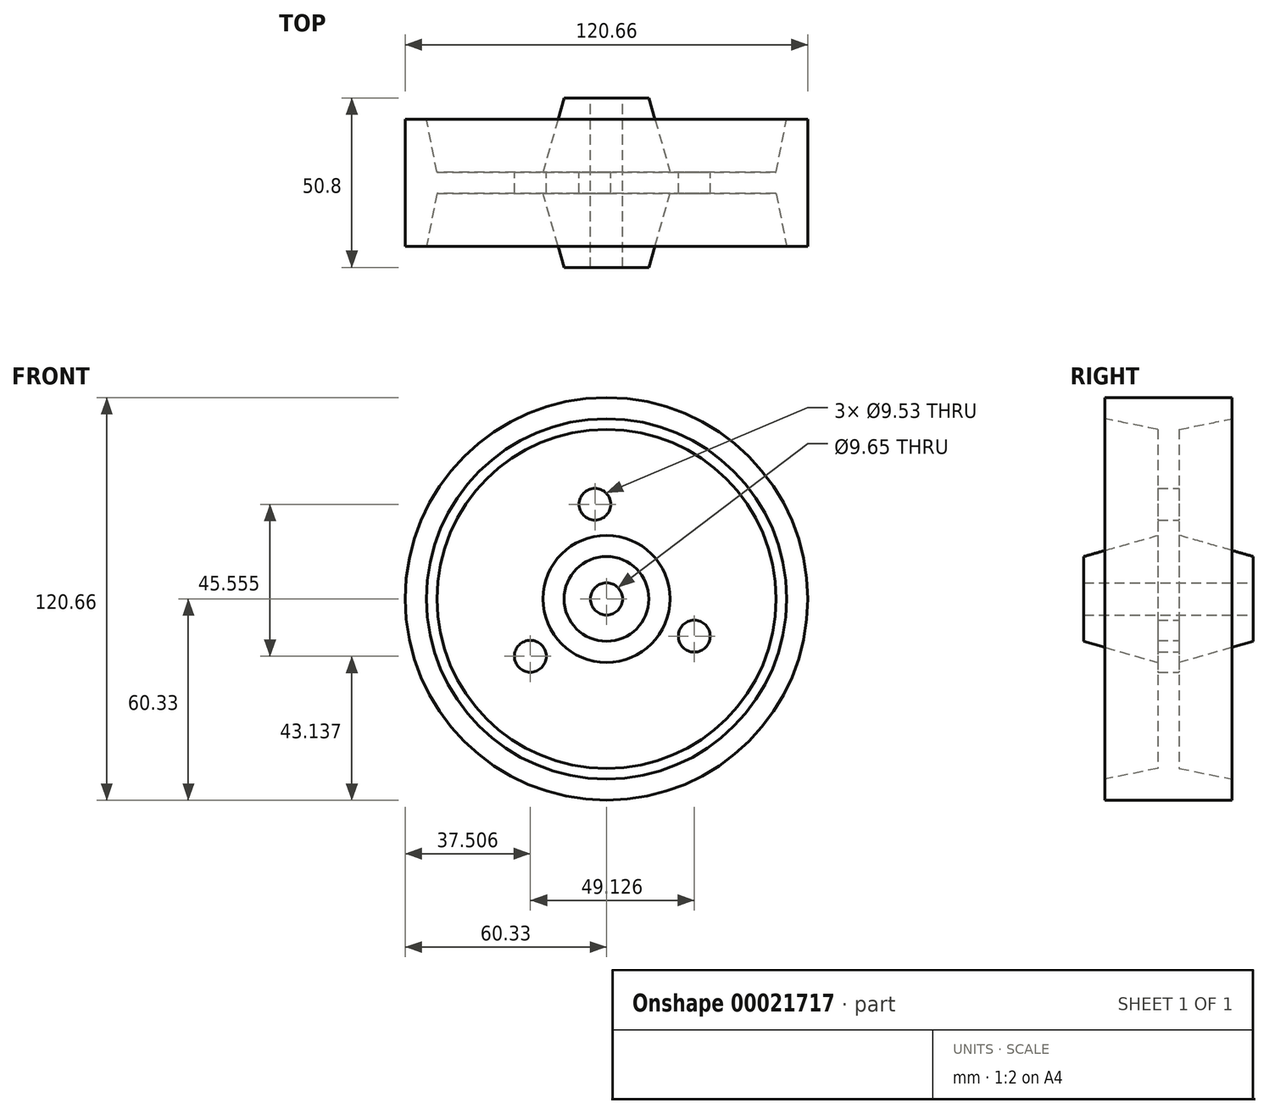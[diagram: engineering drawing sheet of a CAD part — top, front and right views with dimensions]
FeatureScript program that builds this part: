
annotation { "Feature Type Name" : "Feature", "Feature Type Description" : "" }
export const myFeature = defineFeature(function(context is Context, id is Id, definition is map)
    precondition{}
    {
        {
            var Q0;
            Q0=qCreatedBy(makeId("Right.planeOp"),FACE);
            var sketch = newSketch(context, id + "F0", { "sketchPlane" : qUnion([Q0])});
            skLineSegment(sketch, "E0", {"start": v(0, 0) * mm, "end": v(-50.8, 0) * mm});
            skLineSegment(sketch, "E1", {"start": v(-50.8, 0) * mm, "end": v(-50.8, 12.7) * mm});
            skLineSegment(sketch, "E2", {"start": v(-50.8, 12.7) * mm, "end": v(-28.58, 19.05) * mm});
            skLineSegment(sketch, "E3", {"start": v(-22.23, 19.05) * mm, "end": v(0, 12.7) * mm});
            skLineSegment(sketch, "E4", {"start": v(0, 12.7) * mm, "end": v(0, 0) * mm});
            skLineSegment(sketch, "E5", {"start": v(-22.23, 19.05) * mm, "end": v(-22.23, 50.8) * mm});
            skLineSegment(sketch, "E6", {"start": v(-28.58, 19.05) * mm, "end": v(-28.58, 50.8) * mm});
            skLineSegment(sketch, "E7", {"start": v(-44.45, 53.98) * mm, "end": v(-28.58, 50.8) * mm});
            skLineSegment(sketch, "E8", {"start": v(-22.23, 50.8) * mm, "end": v(-6.35, 53.98) * mm});
            skLineSegment(sketch, "E9", {"start": v(-6.35, 53.98) * mm, "end": v(-6.35, 60.33) * mm});
            skLineSegment(sketch, "E10", {"start": v(-6.35, 60.33) * mm, "end": v(-44.45, 60.33) * mm});
            skLineSegment(sketch, "E11", {"start": v(-44.45, 60.33) * mm, "end": v(-44.45, 53.98) * mm});
            skSolve(sketch);
        }
        {
            var Q0;
            Q0=makeQuery(id+"F0.imprint","IMPRINT",FACE,{"disambiguationData":[TD([[makeQuery(id+"F0.imprint","IMPRINT",EDGE,{"derivedFrom":sQuery(id+"F0.wireOp",EDGE,"E0")}),-1.0]])]});
            var Q1;
            Q1=sQuery(id+"F0.wireOp",EDGE,"E0");
            revolve(context, id + "F1", {"entities" : qUnion([Q0]), "axis" : qUnion([Q1]), "revolveType" : RevolveType.FULL});
        }
        {
            var Q0;
            Q0=qCreatedBy(makeId("Front.planeOp"),FACE);
            var sketch = newSketch(context, id + "F2", { "sketchPlane" : qUnion([Q0])});
            skPoint(sketch, "E12", {"position": v(0, 0) * mm});
            skPoint(sketch, "E13", {"position": v(-3.48, 28.36) * mm});
            skPoint(sketch, "E14", {"position": v(-22.82, -17.2) * mm});
            skPoint(sketch, "E15", {"position": v(26.3, -11.17) * mm});
            skSolve(sketch);
        }
        {
            var Q0;
            Q0=sQuery(id+"F2.wireOp",VERTEX,"E12");
            var Q1;
            Q1=makeQuery(id+"F1.opRevolve","SWEPT_BODY",BODY,{"disambiguationData":[OSD([sQuery(id+"F0.wireOp",EDGE,"E0"),sQuery(id+"F0.wireOp",EDGE,"E1"),sQuery(id+"F0.wireOp",EDGE,"E2"),sQuery(id+"F0.wireOp",EDGE,"E3"),sQuery(id+"F0.wireOp",EDGE,"E4"),sQuery(id+"F0.wireOp",EDGE,"E5"),sQuery(id+"F0.wireOp",EDGE,"E6"),sQuery(id+"F0.wireOp",EDGE,"E7"),sQuery(id+"F0.wireOp",EDGE,"E8"),sQuery(id+"F0.wireOp",EDGE,"E9"),sQuery(id+"F0.wireOp",EDGE,"E10"),sQuery(id+"F0.wireOp",EDGE,"E11")])]});
            hole(context, id + "F3", {"style" : HoleStyle.SIMPLE, "holeDiameter" : 9.65 * mm, "endStyle" : HoleEndStyle.THROUGH, "oppositeDirection" : true, "locations" : qUnion([Q0]), "scope" : qUnion([Q1])});
        }
        {
            var Q0;
            Q0=sQuery(id+"F2.wireOp",VERTEX,"E13");
            var Q1;
            Q1=sQuery(id+"F2.wireOp",VERTEX,"E14");
            var Q2;
            Q2=sQuery(id+"F2.wireOp",VERTEX,"E15");
            var Q3;
            Q3=makeQuery(id+"F1.opRevolve","SWEPT_BODY",BODY,{"disambiguationData":[OSD([sQuery(id+"F0.wireOp",EDGE,"E0"),sQuery(id+"F0.wireOp",EDGE,"E1"),sQuery(id+"F0.wireOp",EDGE,"E2"),sQuery(id+"F0.wireOp",EDGE,"E3"),sQuery(id+"F0.wireOp",EDGE,"E4"),sQuery(id+"F0.wireOp",EDGE,"E5"),sQuery(id+"F0.wireOp",EDGE,"E6"),sQuery(id+"F0.wireOp",EDGE,"E7"),sQuery(id+"F0.wireOp",EDGE,"E8"),sQuery(id+"F0.wireOp",EDGE,"E9"),sQuery(id+"F0.wireOp",EDGE,"E10"),sQuery(id+"F0.wireOp",EDGE,"E11")])]});
            hole(context, id + "F4", {"style" : HoleStyle.SIMPLE, "holeDiameter" : 9.52 * mm, "endStyle" : HoleEndStyle.THROUGH, "oppositeDirection" : true, "locations" : qUnion([Q0, Q1, Q2]), "scope" : qUnion([Q3])});
        }
    });
